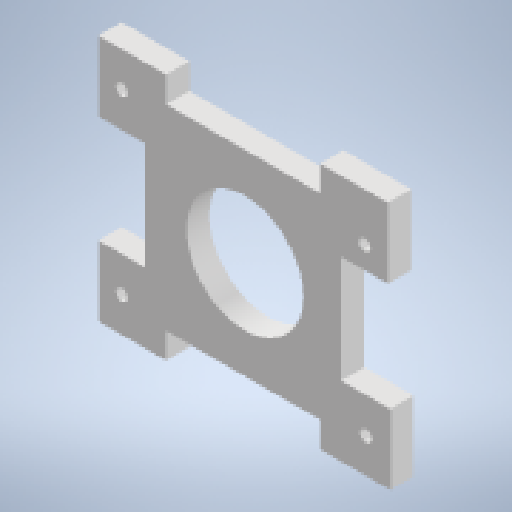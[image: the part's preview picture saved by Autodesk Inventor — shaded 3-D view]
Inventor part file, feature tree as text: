
AUTODESK INVENTOR PART (.ipt)
format: ipt  version: 2023 (Build 270158000, 158)  size: 185,856 bytes
history: native  units: mm
features: reference x5, other x4, sketch x1, extrude x1
ambient origin geometry x8: Origin, YZ Plane, XZ Plane, XY Plane, X Axis, Y Axis, Z Axis, Center Point
bodies: Solid1 (feature_tree)
feature tree (11):
  sketch  "Sketch2"  dims[d1=5.0mm d2=0.0mm]
  extrude  "Extrusion1"  [1 undecoded]
  reference  "Reference8"
  reference  "Reference9"
  reference  "Reference10"
  reference  "Reference11"
  reference  "Reference12"
  other  "<userpath>\OneDrive\Namizje\school\4. letnik\Matura\Izdelovanje\3D model\3D_skenner.iam"
  other  "3D_skenner.iam"
  other  "Ogrodje_spodaj_1:1"
  other  "motor_sample:1"
note: 1 required parameter value undecoded (feature->parameter linkage not recoverable at this tier; creation-order binding heuristic only, values carry confidence <= 0.55)
